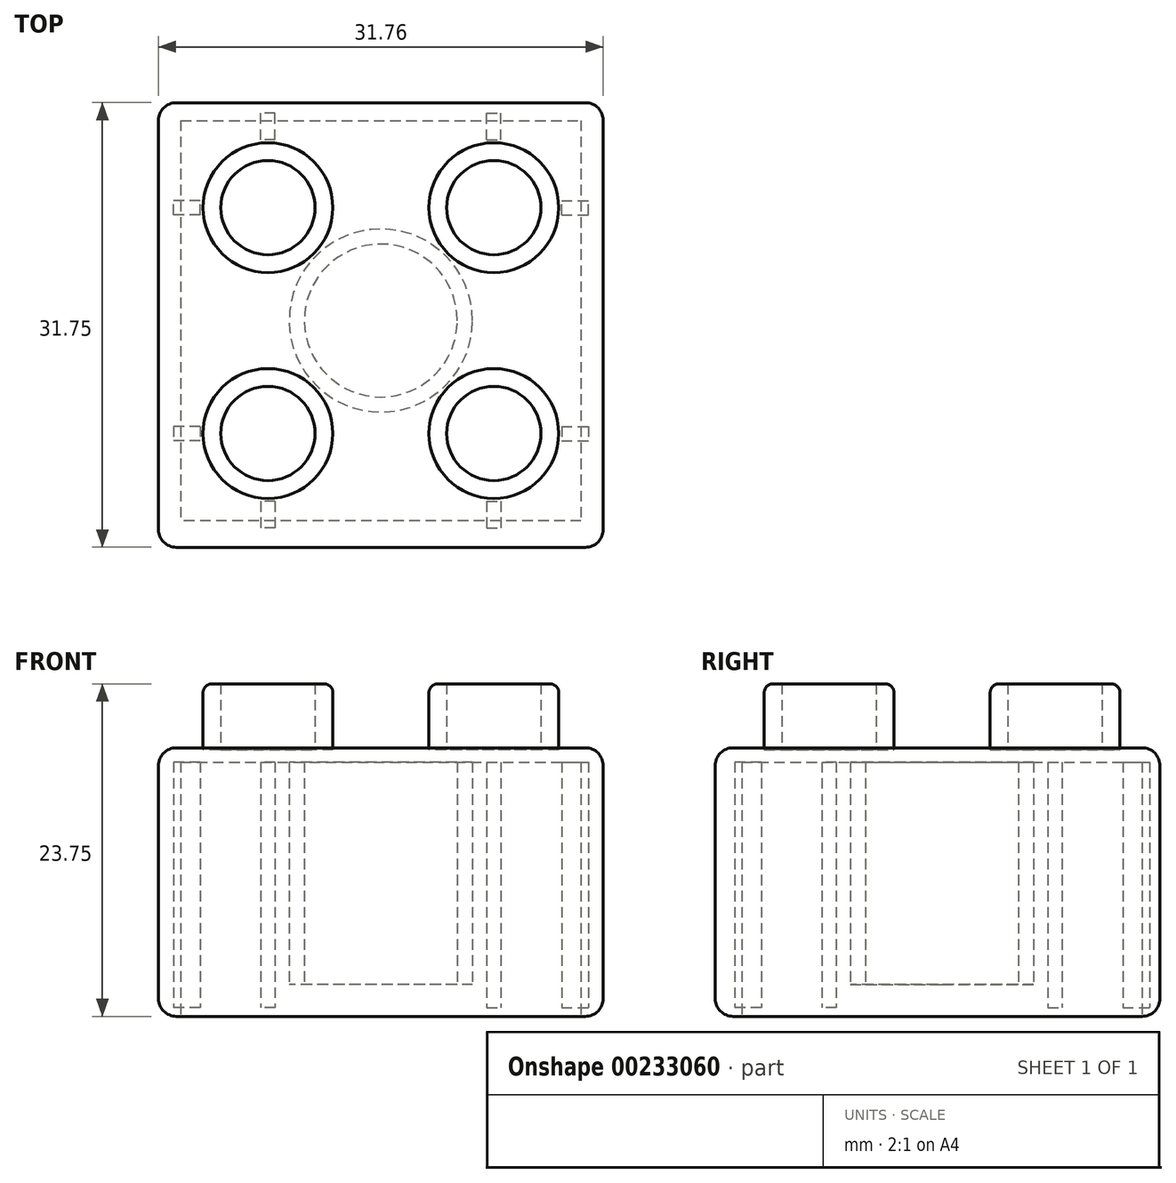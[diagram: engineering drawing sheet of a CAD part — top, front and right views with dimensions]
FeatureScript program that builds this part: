
annotation { "Feature Type Name" : "Feature", "Feature Type Description" : "" }
export const myFeature = defineFeature(function(context is Context, id is Id, definition is map)
    precondition{}
    {
        {
            var Q0;
            Q0=qCreatedBy(makeId("Top.planeOp"),FACE);
            var sketch = newSketch(context, id + "F0", { "sketchPlane" : qUnion([Q0])});
            skPoint(sketch, "E0", {"position": v(0, 16.87) * mm});
            skPoint(sketch, "E1", {"position": v(0, 15.88) * mm});
            skPoint(sketch, "E2", {"position": v(0, -14.88) * mm});
            skPoint(sketch, "E3", {"position": v(0, -15.88) * mm});
            skPoint(sketch, "E4", {"position": v(17.1, 0) * mm});
            skPoint(sketch, "E5", {"position": v(15.88, 0) * mm});
            skPoint(sketch, "E6", {"position": v(-15.88, 0) * mm});
            skPoint(sketch, "E7", {"position": v(15.64, 15.88) * mm});
            skPoint(sketch, "E8", {"position": v(15.88, 15.56) * mm});
            skPoint(sketch, "E9", {"position": v(-16.3, -15.88) * mm});
            skPoint(sketch, "E10", {"position": v(-15.88, -16.2) * mm});
            skLineSegment(sketch, "E11.bottom", {"start": v(-15.88, -16.2) * mm, "end": v(15.88, -16.2) * mm});
            skLineSegment(sketch, "E11.top", {"start": v(-15.88, 15.56) * mm, "end": v(15.88, 15.56) * mm});
            skLineSegment(sketch, "E11.left", {"start": v(-15.88, -16.2) * mm, "end": v(-15.88, 15.56) * mm});
            skLineSegment(sketch, "E11.right", {"start": v(15.88, -16.2) * mm, "end": v(15.88, 15.56) * mm});
            skSolve(sketch);
        }
        {
            var Q0;
            Q0=makeQuery(id+"F0.imprint","IMPRINT",FACE,{"disambiguationData":[TD([[makeQuery(id+"F0.imprint","IMPRINT",EDGE,{"derivedFrom":sQuery(id+"F0.wireOp",EDGE,"E11.bottom")}),1.0]])]});
            var sketch = newSketch(context, id + "F1", { "sketchPlane" : qUnion([Q0])});
            skPoint(sketch, "E12", {"position": v(14.77, 0) * mm});
            skPoint(sketch, "E13", {"position": v(14.29, 0) * mm});
            skPoint(sketch, "E14", {"position": v(-14.29, 0) * mm});
            skPoint(sketch, "E15", {"position": v(-14.29, -14.92) * mm});
            skPoint(sketch, "E16", {"position": v(-14.29, -14.29) * mm});
            skPoint(sketch, "E17", {"position": v(14.29, 14.33) * mm});
            skPoint(sketch, "E18", {"position": v(14.29, 14.29) * mm});
            skLineSegment(sketch, "E19.bottom", {"start": v(-14.29, -14.29) * mm, "end": v(14.29, -14.29) * mm});
            skLineSegment(sketch, "E19.top", {"start": v(-14.29, 14.29) * mm, "end": v(14.29, 14.29) * mm});
            skLineSegment(sketch, "E19.left", {"start": v(-14.29, -14.29) * mm, "end": v(-14.29, 14.29) * mm});
            skLineSegment(sketch, "E19.right", {"start": v(14.29, -14.29) * mm, "end": v(14.29, 14.29) * mm});
            skSolve(sketch);
        }
        {
            var Q0;
            Q0=makeQuery(id+"F1.imprint","IMPRINT",FACE,{"disambiguationData":[TD([[makeQuery(id+"F1.imprint","IMPRINT",EDGE,{"derivedFrom":sQuery(id+"F1.wireOp",EDGE,"E19.bottom")}),1.0]])]});
            var sketch = newSketch(context, id + "F2", { "sketchPlane" : qUnion([Q0])});
            skPoint(sketch, "E20", {"position": v(0, 0) * mm});
            skCircle(sketch, "E21", {"center": v(0, 0) * mm, "radius": 6.54 * mm});
            skSolve(sketch);
        }
        {
            var Q0;
            Q0=makeQuery(id+"F1.imprint","IMPRINT",FACE,{"disambiguationData":[TD([[makeQuery(id+"F1.imprint","IMPRINT",EDGE,{"derivedFrom":sQuery(id+"F1.wireOp",EDGE,"E19.bottom")}),1.0]])]});
            var sketch = newSketch(context, id + "F3", { "sketchPlane" : qUnion([Q0])});
            skPoint(sketch, "E22", {"position": v(0, 0) * mm});
            skCircle(sketch, "E23", {"center": v(0, 0) * mm, "radius": 5.46 * mm});
            skSolve(sketch);
        }
        {
            var Q0;
            Q0=makeQuery(id+"F1.imprint","IMPRINT",FACE,{"disambiguationData":[TD([[makeQuery(id+"F1.imprint","IMPRINT",EDGE,{"derivedFrom":sQuery(id+"F1.wireOp",EDGE,"E19.bottom")}),1.0]])]});
            var sketch = newSketch(context, id + "F4", { "sketchPlane" : qUnion([Q0])});
            skPoint(sketch, "E24", {"position": v(0, 1.02) * mm});
            skPoint(sketch, "E25", {"position": v(0, 0.95) * mm});
            skPoint(sketch, "E26", {"position": v(0, -0.95) * mm});
            skPoint(sketch, "E27", {"position": v(-0.23, 0) * mm});
            skPoint(sketch, "E28", {"position": v(-0.5, 0) * mm});
            skPoint(sketch, "E29", {"position": v(0.3, 0) * mm});
            skPoint(sketch, "E30", {"position": v(0.5, 0) * mm});
            skPoint(sketch, "E31", {"position": v(-0.5, -0.86) * mm});
            skPoint(sketch, "E32", {"position": v(-0.5, -0.95) * mm});
            skPoint(sketch, "E33", {"position": v(0.5, 0.95) * mm});
            skLineSegment(sketch, "E34.bottom", {"start": v(-0.5, -0.95) * mm, "end": v(0.5, -0.95) * mm});
            skLineSegment(sketch, "E34.top", {"start": v(-0.5, 0.95) * mm, "end": v(0.5, 0.95) * mm});
            skLineSegment(sketch, "E34.left", {"start": v(-0.5, -0.95) * mm, "end": v(-0.5, 0.95) * mm});
            skLineSegment(sketch, "E34.right", {"start": v(0.5, -0.95) * mm, "end": v(0.5, 0.95) * mm});
            skSolve(sketch);
        }
        {
            var Q0;
            Q0=qSketchRegion(id+"F0",true);
            extrude(context, id + "F5", {"entities" : qUnion([Q0]), "depth" : 19.18 * mm});
        }
        {
            var Q0;
            Q0=qSketchRegion(id+"F1",true);
            extrude(context, id + "F6", {"entities" : qUnion([Q0]), "operationType" : NewBodyOperationType.REMOVE, "depth" : 18.16 * mm, "hasSecondDirection" : true, "secondDirectionOppositeDirection" : true, "secondDirectionDepth" : 0.38 * mm});
        }
        {
            var Q0;
            Q0=qSketchRegion(id+"F2",true);
            extrude(context, id + "F7", {"entities" : qUnion([Q0]), "operationType" : NewBodyOperationType.ADD, "depth" : 15.88 * mm});
        }
        {
            var Q0;
            Q0=qSketchRegion(id+"F3",true);
            extrude(context, id + "F8", {"entities" : qUnion([Q0]), "operationType" : NewBodyOperationType.REMOVE, "depth" : 15.88 * mm, "hasSecondDirection" : true, "secondDirectionOppositeDirection" : true, "secondDirectionDepth" : 0.64 * mm});
        }
        {
            var Q0;
            Q0=makeQuery(id+"F7.opExtrude","SWEPT_BODY",BODY,{"disambiguationData":[OSD([sQuery(id+"F2.wireOp",EDGE,"E21")])]});
            transform(context, id + "F9", {"entities" : qUnion([Q0]), "transformType" : TransformType.TRANSLATION_3D, "dx" : 0 * mm, "dy" : 0 * mm, "dz" : 2.3 * mm, "makeCopy" : false});
        }
        {
            var Q0;
            Q0=makeQuery(id+"F4.imprint","IMPRINT",FACE,{"disambiguationData":[TD([[makeQuery(id+"F4.imprint","IMPRINT",EDGE,{"derivedFrom":sQuery(id+"F4.wireOp",EDGE,"E34.bottom")}),1.0]])]});
            extrude(context, id + "F10", {"entities" : qUnion([Q0]), "operationType" : NewBodyOperationType.ADD, "depth" : 17.53 * mm});
        }
        {
            var Q0;
            Q0=makeQuery(id+"F10.opExtrude","SWEPT_BODY",BODY,{"disambiguationData":[OSD([sQuery(id+"F4.wireOp",EDGE,"E34.bottom"),sQuery(id+"F4.wireOp",EDGE,"E34.top"),sQuery(id+"F4.wireOp",EDGE,"E34.left"),sQuery(id+"F4.wireOp",EDGE,"E34.right")])]});
            transform(context, id + "F11", {"entities" : qUnion([Q0]), "transformType" : TransformType.TRANSLATION_3D, "dx" : 8.06 * mm, "dy" : 13.86 * mm, "dz" : 0.64 * mm, "makeCopy" : false});
        }
        {
            var Q0;
            Q0=makeQuery(id+"F10.opExtrude","SWEPT_BODY",BODY,{"disambiguationData":[OSD([sQuery(id+"F4.wireOp",EDGE,"E34.bottom"),sQuery(id+"F4.wireOp",EDGE,"E34.top"),sQuery(id+"F4.wireOp",EDGE,"E34.left"),sQuery(id+"F4.wireOp",EDGE,"E34.right")])]});
            var Q1;
            Q1=qCreatedBy(makeId("Front.planeOp"),FACE);
            mirror(context, id + "F12", {"entities" : qUnion([Q0]), "mirrorPlane" : qUnion([Q1])});
        }
        {
            var Q0;
            Q0=makeQuery(id+"F12.opPattern","COPY",BODY,{"derivedFrom":makeQuery(id+"F10.opExtrude","SWEPT_BODY",BODY,{"disambiguationData":[OSD([sQuery(id+"F4.wireOp",EDGE,"E34.bottom"),sQuery(id+"F4.wireOp",EDGE,"E34.top"),sQuery(id+"F4.wireOp",EDGE,"E34.left"),sQuery(id+"F4.wireOp",EDGE,"E34.right")])]}),"instanceName":"1"});
            var Q1;
            Q1=makeQuery(id+"F10.opExtrude","SWEPT_BODY",BODY,{"disambiguationData":[OSD([sQuery(id+"F4.wireOp",EDGE,"E34.bottom"),sQuery(id+"F4.wireOp",EDGE,"E34.top"),sQuery(id+"F4.wireOp",EDGE,"E34.left"),sQuery(id+"F4.wireOp",EDGE,"E34.right")])]});
            var Q2;
            Q2=qCreatedBy(makeId("Right.planeOp"),FACE);
            mirror(context, id + "F13", {"entities" : qUnion([Q0, Q1]), "mirrorPlane" : qUnion([Q2])});
        }
        {
            var Q0;
            Q0=qCreatedBy(makeId("Front.planeOp"),FACE);
            var sketch = newSketch(context, id + "F14", { "sketchPlane" : qUnion([Q0])});
            skLineSegment(sketch, "E35", {"start": v(0, 40.9) * mm, "end": v(0, -32.36) * mm});
            skSolve(sketch);
        }
        {
            var Q0;
            Q0=makeQuery(id+"F12.opPattern","COPY",BODY,{"derivedFrom":makeQuery(id+"F10.opExtrude","SWEPT_BODY",BODY,{"disambiguationData":[OSD([sQuery(id+"F4.wireOp",EDGE,"E34.bottom"),sQuery(id+"F4.wireOp",EDGE,"E34.top"),sQuery(id+"F4.wireOp",EDGE,"E34.left"),sQuery(id+"F4.wireOp",EDGE,"E34.right")])]}),"instanceName":"1"});
            var Q1;
            Q1=makeQuery(id+"F13.opPattern","COPY",BODY,{"derivedFrom":makeQuery(id+"F12.opPattern","COPY",BODY,{"derivedFrom":makeQuery(id+"F10.opExtrude","SWEPT_BODY",BODY,{"disambiguationData":[OSD([sQuery(id+"F4.wireOp",EDGE,"E34.bottom"),sQuery(id+"F4.wireOp",EDGE,"E34.top"),sQuery(id+"F4.wireOp",EDGE,"E34.left"),sQuery(id+"F4.wireOp",EDGE,"E34.right")])]}),"instanceName":"1"}),"instanceName":"1"});
            var Q2;
            Q2=makeQuery(id+"F10.opExtrude","SWEPT_BODY",BODY,{"disambiguationData":[OSD([sQuery(id+"F4.wireOp",EDGE,"E34.bottom"),sQuery(id+"F4.wireOp",EDGE,"E34.top"),sQuery(id+"F4.wireOp",EDGE,"E34.left"),sQuery(id+"F4.wireOp",EDGE,"E34.right")])]});
            var Q3;
            Q3=makeQuery(id+"F13.opPattern","COPY",BODY,{"derivedFrom":makeQuery(id+"F10.opExtrude","SWEPT_BODY",BODY,{"disambiguationData":[OSD([sQuery(id+"F4.wireOp",EDGE,"E34.bottom"),sQuery(id+"F4.wireOp",EDGE,"E34.top"),sQuery(id+"F4.wireOp",EDGE,"E34.left"),sQuery(id+"F4.wireOp",EDGE,"E34.right")])]}),"instanceName":"1"});
            var Q4;
            Q4=sQuery(id+"F14.wireOp",EDGE,"E35");
            transform(context, id + "F15", {"entities" : qUnion([Q0, Q1, Q2, Q3]), "transformType" : TransformType.ROTATION, "transformAxis" : qUnion([Q4]), "angle" : 90 * degree, "makeCopy" : true});
        }
        {
            var Q0;
            Q0=qCreatedBy(makeId("Top.planeOp"),FACE);
            var sketch = newSketch(context, id + "F16", { "sketchPlane" : qUnion([Q0])});
            skCircle(sketch, "E36", {"center": v(0, 0) * mm, "radius": 4.64 * mm});
            skSolve(sketch);
        }
        {
            var Q0;
            Q0=qCreatedBy(makeId("Top.planeOp"),FACE);
            var sketch = newSketch(context, id + "F17", { "sketchPlane" : qUnion([Q0])});
            skCircle(sketch, "E37", {"center": v(0, 0) * mm, "radius": 3.37 * mm});
            skSolve(sketch);
        }
        {
            var Q0;
            Q0=makeQuery(id+"F16.imprint","IMPRINT",FACE,{"disambiguationData":[TD([[makeQuery(id+"F16.imprint","IMPRINT",EDGE,{"derivedFrom":sQuery(id+"F16.wireOp",EDGE,"E36")}),1.0]])]});
            extrude(context, id + "F18", {"entities" : qUnion([Q0]), "depth" : 4.7 * mm});
        }
        {
            var Q0;
            Q0=makeQuery(id+"F17.imprint","IMPRINT",FACE,{"disambiguationData":[TD([[makeQuery(id+"F17.imprint","IMPRINT",EDGE,{"derivedFrom":sQuery(id+"F17.wireOp",EDGE,"E37")}),1.0]])]});
            extrude(context, id + "F19", {"entities" : qUnion([Q0]), "operationType" : NewBodyOperationType.REMOVE, "depth" : 4.7 * mm});
        }
        {
            var Q0;
            Q0=makeQuery(id+"F18.opExtrude","SWEPT_BODY",BODY,{"disambiguationData":[OSD([sQuery(id+"F16.wireOp",EDGE,"E36")])]});
            transform(context, id + "F20", {"entities" : qUnion([Q0]), "transformType" : TransformType.TRANSLATION_3D, "dx" : 8.06 * mm, "dy" : 8.06 * mm, "dz" : 19.05 * mm, "makeCopy" : false});
        }
        {
            var Q0;
            Q0=makeQuery(id+"F18.opExtrude","SWEPT_BODY",BODY,{"disambiguationData":[OSD([sQuery(id+"F16.wireOp",EDGE,"E36")])]});
            var Q1;
            Q1=qCreatedBy(makeId("Front.planeOp"),FACE);
            mirror(context, id + "F21", {"entities" : qUnion([Q0]), "mirrorPlane" : qUnion([Q1])});
        }
        {
            var Q0;
            Q0=makeQuery(id+"F18.opExtrude","SWEPT_BODY",BODY,{"disambiguationData":[OSD([sQuery(id+"F16.wireOp",EDGE,"E36")])]});
            var Q1;
            Q1=makeQuery(id+"F21.opPattern","COPY",BODY,{"derivedFrom":makeQuery(id+"F18.opExtrude","SWEPT_BODY",BODY,{"disambiguationData":[OSD([sQuery(id+"F16.wireOp",EDGE,"E36")])]}),"instanceName":"1"});
            var Q2;
            Q2=qCreatedBy(makeId("Right.planeOp"),FACE);
            mirror(context, id + "F22", {"entities" : qUnion([Q0, Q1]), "mirrorPlane" : qUnion([Q2])});
        }
        {
            var Q0;
            Q0=makeQuery(id+"F5.opExtrude","CAP_EDGE",EDGE,{"disambiguationData":[OSD([sQuery(id+"F0.wireOp",EDGE,"E11.bottom")])],"isStart":false});
            var Q1;
            Q1=makeQuery(id+"F5.opExtrude","CAP_EDGE",EDGE,{"disambiguationData":[OSD([sQuery(id+"F0.wireOp",EDGE,"E11.left")])],"isStart":false});
            var Q2;
            Q2=makeQuery(id+"F5.opExtrude","CAP_EDGE",EDGE,{"disambiguationData":[OSD([sQuery(id+"F0.wireOp",EDGE,"E11.top")])],"isStart":false});
            var Q3;
            Q3=makeQuery(id+"F5.opExtrude","CAP_EDGE",EDGE,{"disambiguationData":[OSD([sQuery(id+"F0.wireOp",EDGE,"E11.right")])],"isStart":false});
            var Q4;
            Q4=makeQuery(id+"F5.opExtrude","SWEPT_EDGE",EDGE,{"disambiguationData":[OSD([sQuery(id+"F0.wireOp",EDGE,"E11.bottom"),sQuery(id+"F0.wireOp",EDGE,"E11.left")])]});
            var Q5;
            Q5=makeQuery(id+"F5.opExtrude","SWEPT_EDGE",EDGE,{"disambiguationData":[OSD([sQuery(id+"F0.wireOp",EDGE,"E11.bottom"),sQuery(id+"F0.wireOp",EDGE,"E11.right")])]});
            var Q6;
            Q6=makeQuery(id+"F5.opExtrude","SWEPT_EDGE",EDGE,{"disambiguationData":[OSD([sQuery(id+"F0.wireOp",EDGE,"E11.top"),sQuery(id+"F0.wireOp",EDGE,"E11.left")])]});
            var Q7;
            Q7=makeQuery(id+"F5.opExtrude","SWEPT_EDGE",EDGE,{"disambiguationData":[OSD([sQuery(id+"F0.wireOp",EDGE,"E11.top"),sQuery(id+"F0.wireOp",EDGE,"E11.right")])]});
            var Q8;
            Q8=makeQuery(id+"F5.opExtrude","CAP_EDGE",EDGE,{"disambiguationData":[OSD([sQuery(id+"F0.wireOp",EDGE,"E11.right")])],"isStart":true});
            var Q9;
            Q9=makeQuery(id+"F5.opExtrude","CAP_EDGE",EDGE,{"disambiguationData":[OSD([sQuery(id+"F0.wireOp",EDGE,"E11.bottom")])],"isStart":true});
            var Q10;
            Q10=makeQuery(id+"F5.opExtrude","CAP_EDGE",EDGE,{"disambiguationData":[OSD([sQuery(id+"F0.wireOp",EDGE,"E11.left")])],"isStart":true});
            var Q11;
            Q11=makeQuery(id+"F5.opExtrude","CAP_EDGE",EDGE,{"disambiguationData":[OSD([sQuery(id+"F0.wireOp",EDGE,"E11.top")])],"isStart":true});
            fillet(context, id + "F23", {"entities" : qUnion([Q0, Q1, Q2, Q3, Q4, Q5, Q6, Q7, Q8, Q9, Q10, Q11]), "radius" : 1.27 * mm, "tangentPropagation" : true, "allowEdgeOverflow" : false});
        }
        {
            var Q0;
            Q0=makeQuery(id+"F22.opPattern","COPY",EDGE,{"derivedFrom":makeQuery(id+"F18.opExtrude","CAP_EDGE",EDGE,{"disambiguationData":[OSD([sQuery(id+"F16.wireOp",EDGE,"E36")])],"isStart":false}),"instanceName":"1"});
            var Q1;
            Q1=makeQuery(id+"F18.opExtrude","CAP_EDGE",EDGE,{"disambiguationData":[OSD([sQuery(id+"F16.wireOp",EDGE,"E36")])],"isStart":false});
            var Q2;
            Q2=makeQuery(id+"F21.opPattern","COPY",EDGE,{"derivedFrom":makeQuery(id+"F18.opExtrude","CAP_EDGE",EDGE,{"disambiguationData":[OSD([sQuery(id+"F16.wireOp",EDGE,"E36")])],"isStart":false}),"instanceName":"1"});
            var Q3;
            Q3=makeQuery(id+"F22.opPattern","COPY",EDGE,{"derivedFrom":makeQuery(id+"F21.opPattern","COPY",EDGE,{"derivedFrom":makeQuery(id+"F18.opExtrude","CAP_EDGE",EDGE,{"disambiguationData":[OSD([sQuery(id+"F16.wireOp",EDGE,"E36")])],"isStart":false}),"instanceName":"1"}),"instanceName":"1"});
            fillet(context, id + "F24", {"entities" : qUnion([Q0, Q1, Q2, Q3]), "radius" : 0.64 * mm, "tangentPropagation" : true, "allowEdgeOverflow" : false});
        }
    });
